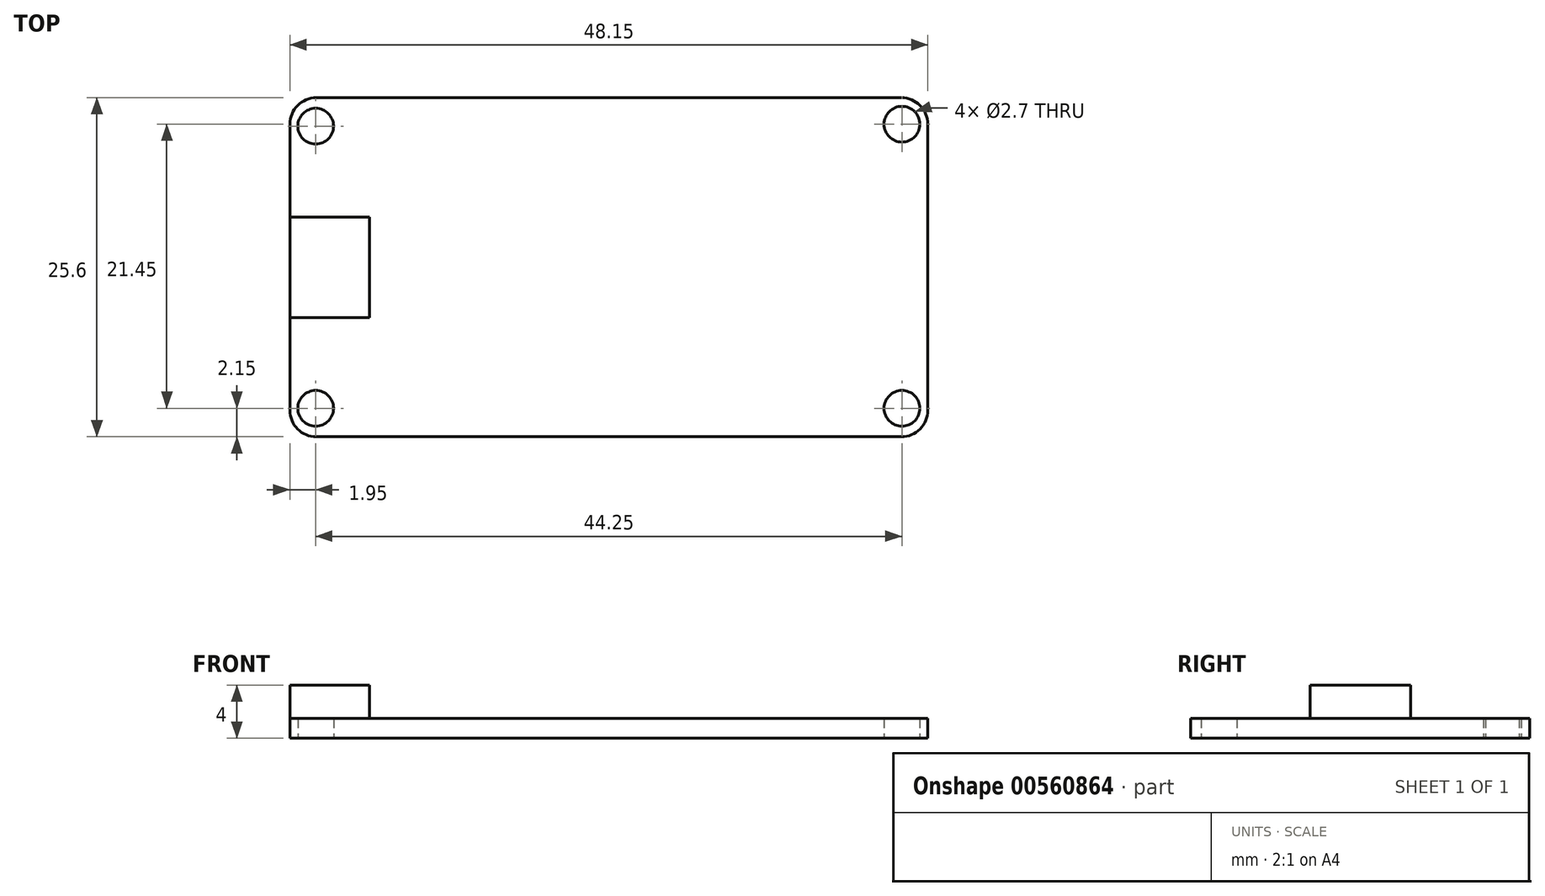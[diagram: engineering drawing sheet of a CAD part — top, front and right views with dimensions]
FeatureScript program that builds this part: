
annotation { "Feature Type Name" : "Feature", "Feature Type Description" : "" }
export const myFeature = defineFeature(function(context is Context, id is Id, definition is map)
    precondition{}
    {
        {
            var Q0;
            Q0=qCreatedBy(makeId("Top.planeOp"),FACE);
            var sketch = newSketch(context, id + "F0", { "sketchPlane" : qUnion([Q0])});
            skLineSegment(sketch, "E0.bottom", {"start": v(2, 0) * mm, "end": v(46.15, 0) * mm});
            skLineSegment(sketch, "E0.top", {"start": v(2, 25.6) * mm, "end": v(46.15, 25.6) * mm});
            skLineSegment(sketch, "E0.left", {"start": v(0, 2) * mm, "end": v(0, 23.6) * mm});
            skLineSegment(sketch, "E0.right", {"start": v(48.15, 2) * mm, "end": v(48.15, 23.6) * mm});
            skPoint(sketch, "E1.visualSharp", {"position": v(0, 25.6) * mm});
            skArc(sketch, "E1.filletArc", {"start": v(2, 25.6) * mm, "mid": v(0.59, 25.01) * mm, "end": v(0, 23.6) * mm});
            skPoint(sketch, "E2.visualSharp", {"position": v(48.15, 25.6) * mm});
            skArc(sketch, "E2.filletArc", {"start": v(48.15, 23.6) * mm, "mid": v(47.56, 25.01) * mm, "end": v(46.15, 25.6) * mm});
            skPoint(sketch, "E3.visualSharp", {"position": v(48.15, 0) * mm});
            skArc(sketch, "E3.filletArc", {"start": v(46.15, 0) * mm, "mid": v(47.56, 0.59) * mm, "end": v(48.15, 2) * mm});
            skPoint(sketch, "E4.visualSharp", {"position": v(0, 0) * mm});
            skArc(sketch, "E4.filletArc", {"start": v(0, 2) * mm, "mid": v(0.59, 0.59) * mm, "end": v(2, 0) * mm});
            skCircle(sketch, "E5", {"center": v(1.95, 23.45) * mm, "radius": 1.35 * mm});
            skCircle(sketch, "E6", {"center": v(46.2, 23.6) * mm, "radius": 1.35 * mm});
            skCircle(sketch, "E7", {"center": v(46.2, 2.15) * mm, "radius": 1.35 * mm});
            skCircle(sketch, "E8", {"center": v(1.95, 2.15) * mm, "radius": 1.35 * mm});
            skSolve(sketch);
        }
        {
            var Q0;
            Q0=makeQuery(id+"F0.imprint","IMPRINT",FACE,{"disambiguationData":[TD([[makeQuery(id+"F0.imprint","IMPRINT",EDGE,{"derivedFrom":sQuery(id+"F0.wireOp",EDGE,"E0.bottom")}),1.0]])]});
            extrude(context, id + "F1", {"entities" : qUnion([Q0]), "depth" : 1.5 * mm, "offsetDistance" : 25 * mm});
        }
        {
            var Q0;
            Q0=makeQuery(id+"F1.opExtrude","CAP_FACE",FACE,{"disambiguationData":[OSD([sQuery(id+"F0.wireOp",EDGE,"E0.bottom"),sQuery(id+"F0.wireOp",EDGE,"E0.top"),sQuery(id+"F0.wireOp",EDGE,"E0.left"),sQuery(id+"F0.wireOp",EDGE,"E0.right"),sQuery(id+"F0.wireOp",EDGE,"E1.filletArc"),sQuery(id+"F0.wireOp",EDGE,"E2.filletArc"),sQuery(id+"F0.wireOp",EDGE,"E3.filletArc"),sQuery(id+"F0.wireOp",EDGE,"E4.filletArc"),sQuery(id+"F0.wireOp",EDGE,"E5"),sQuery(id+"F0.wireOp",EDGE,"E6"),sQuery(id+"F0.wireOp",EDGE,"E7"),sQuery(id+"F0.wireOp",EDGE,"E8")])],"isStart":false});
            var sketch = newSketch(context, id + "F2", { "sketchPlane" : qUnion([Q0])});
            skLineSegment(sketch, "E9.bottom", {"start": v(0, 16.6) * mm, "end": v(6, 16.6) * mm});
            skLineSegment(sketch, "E9.top", {"start": v(0, 9) * mm, "end": v(6, 9) * mm});
            skLineSegment(sketch, "E9.left", {"start": v(0, 16.6) * mm, "end": v(0, 9) * mm});
            skLineSegment(sketch, "E9.right", {"start": v(6, 16.6) * mm, "end": v(6, 9) * mm});
            skSolve(sketch);
        }
        {
            var Q0;
            Q0=makeQuery(id+"F2.imprint","IMPRINT",FACE,{"disambiguationData":[TD([[makeQuery(id+"F2.imprint","IMPRINT",EDGE,{"derivedFrom":sQuery(id+"F2.wireOp",EDGE,"E9.bottom")}),-1.0]])]});
            extrude(context, id + "F3", {"entities" : qUnion([Q0]), "operationType" : NewBodyOperationType.ADD, "depth" : 2.5 * mm, "offsetDistance" : 25 * mm});
        }
    });
